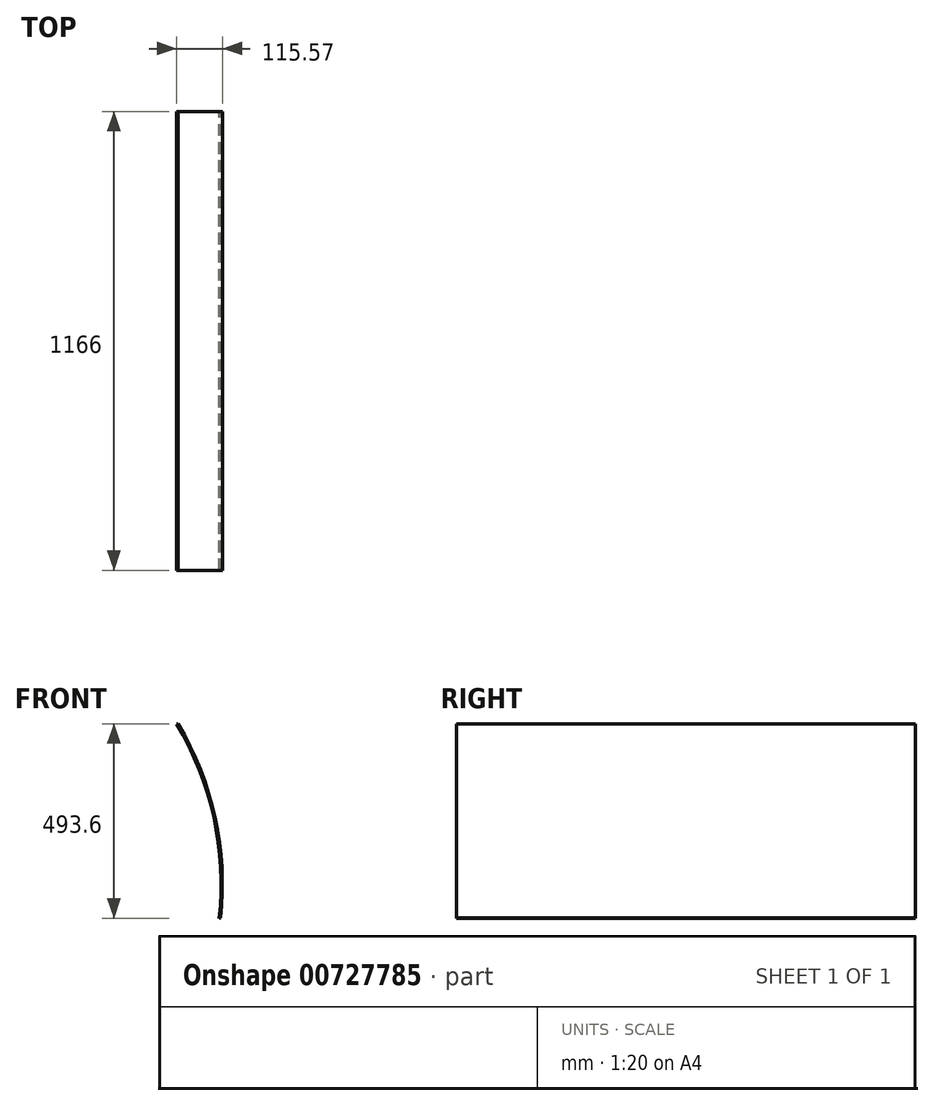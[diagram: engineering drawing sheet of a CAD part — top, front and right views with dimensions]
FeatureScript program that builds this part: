
annotation { "Feature Type Name" : "Feature", "Feature Type Description" : "" }
export const myFeature = defineFeature(function(context is Context, id is Id, definition is map)
    precondition{}
    {
        {
            var Q0;
            Q0=qCreatedBy(makeId("Front.planeOp"),FACE);
            var sketch = newSketch(context, id + "F0", { "sketchPlane" : qUnion([Q0])});
            skArc(sketch, "E0", {"start": v(3, -223.99) * mm, "mid": v(7.34, -160.64) * mm, "end": v(6.63, -97.15) * mm});
            skArc(sketch, "E1", {"start": v(0, -224.07) * mm, "mid": v(-13.79, 31.49) * mm, "end": v(-107.9, 269.48) * mm});
            skLineSegment(sketch, "E2", {"start": v(-107.9, 269.48) * mm, "end": v(-104.38, 269.53) * mm});
            skLineSegment(sketch, "E3", {"start": v(0, -224.07) * mm, "end": v(3, -223.99) * mm});
            skPoint(sketch, "E4", {"position": v(-97.83, 258.3) * mm});
            skPoint(sketch, "E5", {"position": v(-17.28, 59.95) * mm});
            skPoint(sketch, "E6", {"position": v(6.63, -97.22) * mm});
            skArc(sketch, "E7", {"start": v(-63.2, 190.59) * mm, "mid": v(-79.7, 224.86) * mm, "end": v(-97.83, 258.3) * mm});
            skArc(sketch, "E8", {"start": v(-17.65, 61.36) * mm, "mid": v(-37.64, 126.95) * mm, "end": v(-63.2, 190.59) * mm});
            skArc(sketch, "E9", {"start": v(6.63, -97.15) * mm, "mid": v(-1.51, -17.28) * mm, "end": v(-17.65, 61.36) * mm});
            skArc(sketch, "E10", {"start": v(-97.83, 258.3) * mm, "mid": v(-101.08, 263.93) * mm, "end": v(-104.38, 269.53) * mm});
            skSolve(sketch);
        }
        {
            var Q0;
            Q0=makeQuery(id+"F0.imprint","IMPRINT",FACE,{"disambiguationData":[TD([[makeQuery(id+"F0.imprint","IMPRINT",EDGE,{"derivedFrom":sQuery(id+"F0.wireOp",EDGE,"E0")}),1.0]])]});
            extrude(context, id + "F1", {"entities" : qUnion([Q0]), "depth" : 1166 * mm, "offsetDistance" : 25 * mm});
        }
    });
